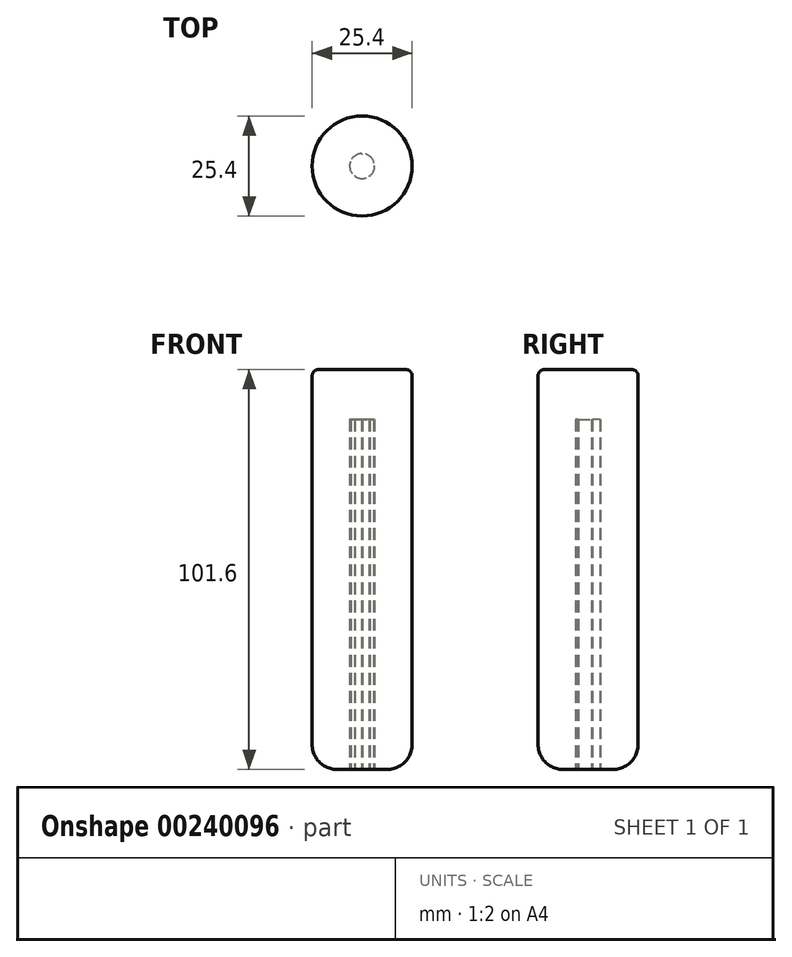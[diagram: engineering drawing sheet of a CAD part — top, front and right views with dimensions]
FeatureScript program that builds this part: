
annotation { "Feature Type Name" : "Feature", "Feature Type Description" : "" }
export const myFeature = defineFeature(function(context is Context, id is Id, definition is map)
    precondition{}
    {
        {
            var Q0;
            Q0=qCreatedBy(makeId("Top.planeOp"),FACE);
            var sketch = newSketch(context, id + "F0", { "sketchPlane" : qUnion([Q0])});
            skArc(sketch, "E0", {"start": v(-0.11, 3.17) * mm, "mid": v(-1.87, 2.57) * mm, "end": v(-2.98, 1.09) * mm});
            skCircle(sketch, "E1", {"center": v(0, 0) * mm, "radius": 12.7 * mm});
            skLineSegment(sketch, "E2", {"start": v(0, 3.18) * mm, "end": v(0, 2.98) * mm, "construction": true});
            skLineSegment(sketch, "E3", {"start": v(0, 2.98) * mm, "end": v(-0.11, 3.17) * mm});
            skLineSegment(sketch, "E4", {"start": v(0, 2.98) * mm, "end": v(0.11, 3.17) * mm});
            skLineSegment(sketch, "E5.1.0", {"start": v(-2.83, 0.92) * mm, "end": v(-2.98, 1.09) * mm});
            skLineSegment(sketch, "E5.1.1", {"start": v(-3.02, 0.98) * mm, "end": v(-2.83, 0.92) * mm, "construction": true});
            skLineSegment(sketch, "E5.1.2", {"start": v(-2.83, 0.92) * mm, "end": v(-3.05, 0.87) * mm});
            skLineSegment(sketch, "E5.2.0", {"start": v(-1.75, -2.4) * mm, "end": v(-1.96, -2.5) * mm});
            skLineSegment(sketch, "E5.2.1", {"start": v(-1.87, -2.57) * mm, "end": v(-1.75, -2.4) * mm, "construction": true});
            skLineSegment(sketch, "E5.2.2", {"start": v(-1.75, -2.4) * mm, "end": v(-1.77, -2.63) * mm});
            skLineSegment(sketch, "E5.3.0", {"start": v(1.75, -2.4) * mm, "end": v(1.77, -2.63) * mm});
            skLineSegment(sketch, "E5.3.1", {"start": v(1.87, -2.57) * mm, "end": v(1.75, -2.4) * mm, "construction": true});
            skLineSegment(sketch, "E5.3.2", {"start": v(1.75, -2.4) * mm, "end": v(1.96, -2.5) * mm});
            skLineSegment(sketch, "E5.4.0", {"start": v(2.83, 0.92) * mm, "end": v(3.05, 0.87) * mm});
            skLineSegment(sketch, "E5.4.1", {"start": v(3.02, 0.98) * mm, "end": v(2.83, 0.92) * mm, "construction": true});
            skLineSegment(sketch, "E5.4.2", {"start": v(2.83, 0.92) * mm, "end": v(2.98, 1.09) * mm});
            skArc(sketch, "E6.trimOffspring", {"start": v(2.98, 1.09) * mm, "mid": v(1.87, 2.57) * mm, "end": v(0.11, 3.17) * mm});
            skArc(sketch, "E7.trimOffspring", {"start": v(1.96, -2.5) * mm, "mid": v(3.02, -0.98) * mm, "end": v(3.05, 0.87) * mm});
            skArc(sketch, "E8.trimOffspring", {"start": v(-1.77, -2.63) * mm, "mid": v(0, -3.18) * mm, "end": v(1.77, -2.63) * mm});
            skArc(sketch, "E9.trimOffspring", {"start": v(-3.05, 0.87) * mm, "mid": v(-3.02, -0.98) * mm, "end": v(-1.96, -2.5) * mm});
            skSolve(sketch);
        }
        {
            var Q0;
            Q0=makeQuery(id+"F0.imprint","IMPRINT",FACE,{"disambiguationData":[TD([[makeQuery(id+"F0.imprint","IMPRINT",EDGE,{"derivedFrom":sQuery(id+"F0.wireOp",EDGE,"E0")}),-1.0]])]});
            extrude(context, id + "F1", {"entities" : qUnion([Q0]), "depth" : 88.9 * mm});
        }
        {
            var Q0;
            Q0=makeQuery(id+"F1.opExtrude","CAP_FACE",FACE,{"disambiguationData":[OSD([sQuery(id+"F0.wireOp",EDGE,"E0"),sQuery(id+"F0.wireOp",EDGE,"E1"),sQuery(id+"F0.wireOp",EDGE,"E3"),sQuery(id+"F0.wireOp",EDGE,"E4"),sQuery(id+"F0.wireOp",EDGE,"E5.1.0"),sQuery(id+"F0.wireOp",EDGE,"E5.1.2"),sQuery(id+"F0.wireOp",EDGE,"E5.2.0"),sQuery(id+"F0.wireOp",EDGE,"E5.2.2"),sQuery(id+"F0.wireOp",EDGE,"E5.3.0"),sQuery(id+"F0.wireOp",EDGE,"E5.3.2"),sQuery(id+"F0.wireOp",EDGE,"E5.4.0"),sQuery(id+"F0.wireOp",EDGE,"E5.4.2"),sQuery(id+"F0.wireOp",EDGE,"E6.trimOffspring"),sQuery(id+"F0.wireOp",EDGE,"E7.trimOffspring"),sQuery(id+"F0.wireOp",EDGE,"E8.trimOffspring"),sQuery(id+"F0.wireOp",EDGE,"E9.trimOffspring")])],"isStart":false});
            var sketch = newSketch(context, id + "F2", { "sketchPlane" : qUnion([Q0])});
            skCircle(sketch, "E10.0", {"center": v(0, 0) * mm, "radius": 12.7 * mm});
            skSolve(sketch);
        }
        {
            var Q0;
            Q0=makeQuery(id+"F2.imprint","IMPRINT",FACE,{"disambiguationData":[TD([[makeQuery(id+"F2.imprint","IMPRINT",EDGE,{"derivedFrom":sQuery(id+"F2.wireOp",EDGE,"E10.0")}),1.0]])]});
            var Q1;
            Q1=makeQuery(id+"F2.imprint","IMPRINT",FACE,{"disambiguationData":[TD([[makeQuery(id+"F2.imprint","IMPRINT",EDGE,{"derivedFrom":makeQuery(id+"F1.opExtrude","CAP_EDGE",EDGE,{"disambiguationData":[OSD([sQuery(id+"F0.wireOp",EDGE,"E0")])],"isStart":false})}),1.0]])]});
            extrude(context, id + "F3", {"entities" : qUnion([Q0, Q1]), "operationType" : NewBodyOperationType.ADD, "depth" : 12.7 * mm});
        }
        {
            var Q0;
            Q0=makeQuery(id+"F3.opExtrude","CAP_EDGE",EDGE,{"disambiguationData":[OSD([sQuery(id+"F2.wireOp",EDGE,"E10.0")])],"isStart":false});
            fillet(context, id + "F4", {"entities" : qUnion([Q0]), "radius" : 1.59 * mm, "tangentPropagation" : true, "allowEdgeOverflow" : false});
        }
        {
            var Q0;
            Q0=makeQuery(id+"F1.opExtrude","CAP_EDGE",EDGE,{"disambiguationData":[OSD([sQuery(id+"F0.wireOp",EDGE,"E1")])],"isStart":true});
            fillet(context, id + "F5", {"entities" : qUnion([Q0]), "radius" : 6.35 * mm, "tangentPropagation" : true, "allowEdgeOverflow" : false});
        }
    });
